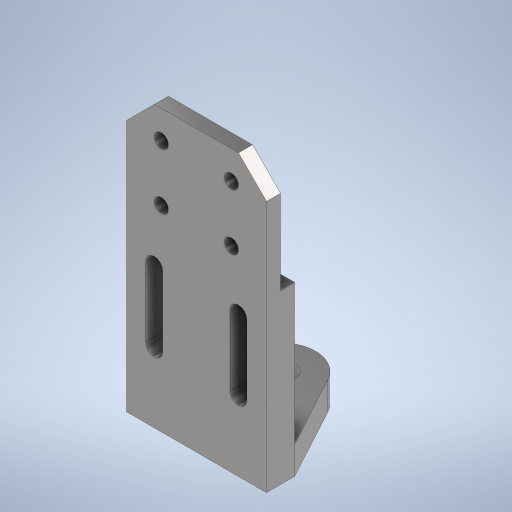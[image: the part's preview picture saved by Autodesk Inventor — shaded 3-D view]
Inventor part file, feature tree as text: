
AUTODESK INVENTOR PART (.ipt)
format: ipt  version: 2024 (Build 280153000, 153)  size: 312,832 bytes
history: native  units: mm
features: sketch x6, extrude x4, hole x2, chamfer x1
ambient origin geometry x8: Origin, YZ Plane, XZ Plane, XY Plane, X Axis, Y Axis, Z Axis, Center Point
bodies: Volumenkörper1 (feature_tree)
feature tree (13):
  extrude  "Extrusion1"  Depth=60.0mm
  extrude  "Extrusion2"  Depth=20.0mm
  extrude  "Extrusion3"  Depth=100.0mm TaperAngle=0.0deg
  extrude  "Extrusion4"  Depth=80.0mm TaperAngle=0.0deg
  chamfer  "Fasen1"  Distance=6.0mm
  hole  "Bohrung1"  [1 undecoded]
  hole  "Bohrung2"  [1 undecoded]
  sketch  "Skizze1"  dims[d0=100.0mm d1=60.0mm]
  sketch  "Skizze2"  dims[d2=50.0mm d4=20.0mm]
  sketch  "Skizze3"  dims[d5=20.0mm d6=0.0mm d7=100.0mm d8=0.0mm]
  sketch  "Skizze4"  dims[d9=10.0mm d10=80.0mm d11=0.0mm]
  sketch  "Skizze5"  dims[d12=60.0mm]
  sketch  "Skizze6"  dims[d13=20.0mm d14=6.0mm d15=50.0mm d16=50.0mm d17=50.0mm d18=80.0mm d19=0.0mm d20=20.0mm d21=2.0mm d22=45.0deg d23=20.0mm d24=40.0mm d25=20.0mm d26=40.0mm d27=25.0mm d28=10.0mm d29=6.0mm d30=4.0mm d31=2.0mm d32=90.0deg d33=8.0mm d34=20.594885mm d35=20.0mm d36=6.0mm d37=4.0mm d38=2.0mm d39=90.0deg d40=8.0mm d41=20.594885mm]
note: 2 required parameter values undecoded (feature->parameter linkage not recoverable at this tier; creation-order binding heuristic only, values carry confidence <= 0.55)
